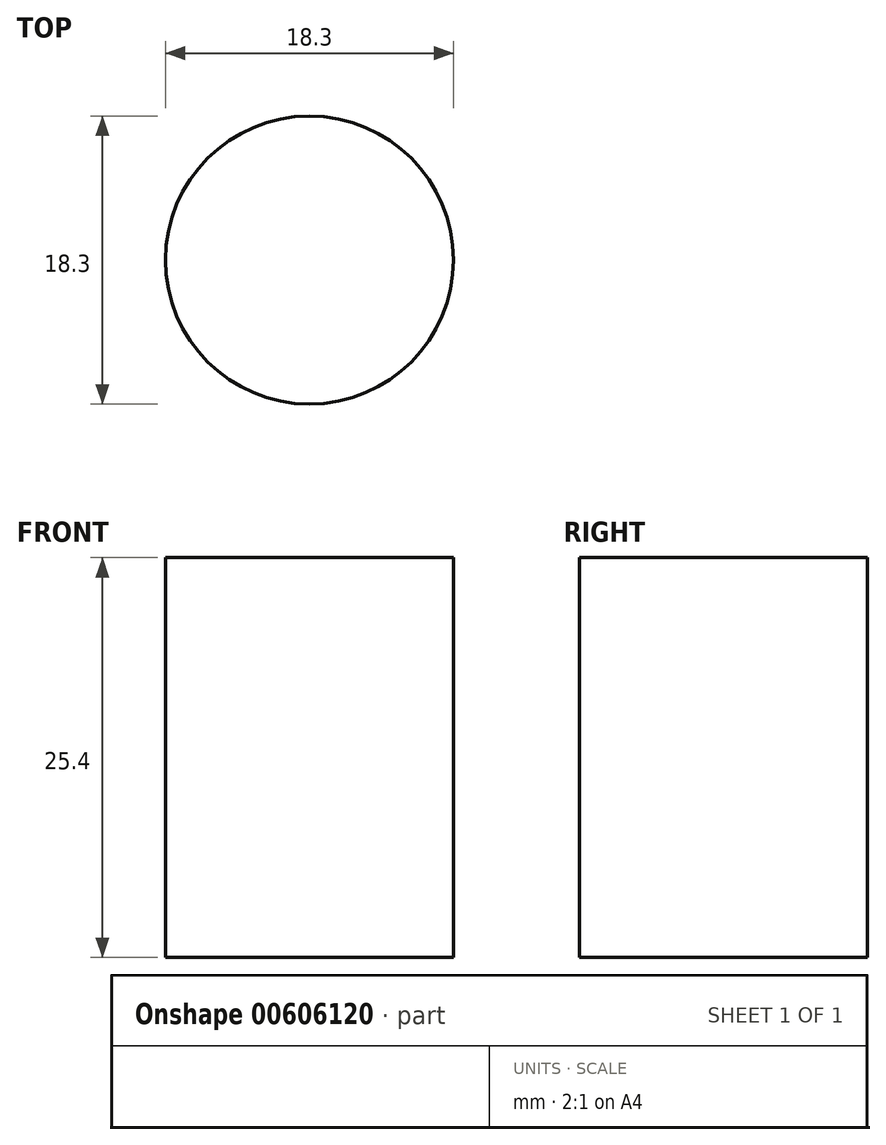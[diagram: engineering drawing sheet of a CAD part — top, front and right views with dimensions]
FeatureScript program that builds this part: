
annotation { "Feature Type Name" : "Feature", "Feature Type Description" : "" }
export const myFeature = defineFeature(function(context is Context, id is Id, definition is map)
    precondition{}
    {
        {
            var Q0;
            Q0=qCreatedBy(makeId("Top.planeOp"),FACE);
            var sketch = newSketch(context, id + "F0", { "sketchPlane" : qUnion([Q0])});
            skCircle(sketch, "E0", {"center": v(0, 0) * mm, "radius": 9.15 * mm});
            skSolve(sketch);
        }
        {
            var Q0;
            Q0=makeQuery(id+"F0.imprint","IMPRINT",FACE,{"disambiguationData":[TD([[makeQuery(id+"F0.imprint","IMPRINT",EDGE,{"derivedFrom":sQuery(id+"F0.wireOp",EDGE,"E0")}),1.0]])]});
            extrude(context, id + "F1", {"entities" : qUnion([Q0]), "depth" : 25.4 * mm, "offsetDistance" : 25.4 * mm});
        }
    });
